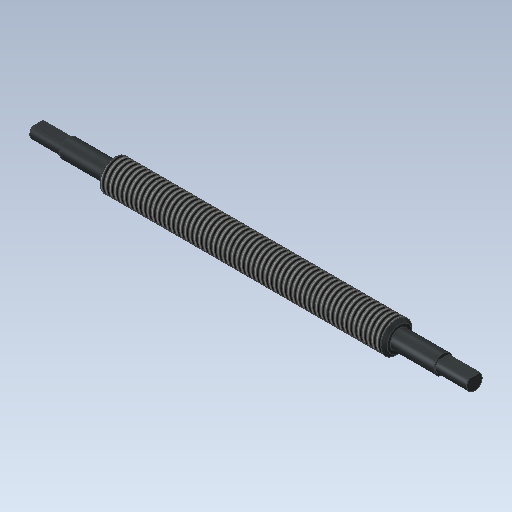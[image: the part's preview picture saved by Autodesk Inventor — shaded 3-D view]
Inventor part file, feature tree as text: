
AUTODESK INVENTOR PART (.ipt)
format: ipt  version: 2020 (Build 240168000, 168)  size: 140,288 bytes
history: native  units: mm
features: extrude x3, sketch x3, thread x1, chamfer x1, mirror x1
ambient origin geometry x8: Origin, YZ Plane, XZ Plane, XY Plane, X Axis, Y Axis, Z Axis, Center Point
bodies: Solid1 (feature_tree)
feature tree (9):
  extrude  "Extrusion1"  Depth=46.0mm TaperAngle=0.0deg
  thread  "Thread1"  [1 undecoded]
  chamfer  "Chamfer1"  Distance=1.0mm Angle=45.0deg
  extrude  "Extrusion2"  Depth=14.0mm TaperAngle=0.0deg
  extrude  "Extrusion3"  Depth=10.0mm
  mirror  "Mirror1"
  sketch  "Sketch1"  dims[d0=10.0mm d1=46.0mm d2=0.0mm d3=10.0mm d4=0.0mm d5=1.0mm d6=2.0mm d7=45.0deg]
  sketch  "Sketch2"  dims[d8=6.0mm d9=14.0mm d10=0.0mm]
  sketch  "Sketch3"  dims[d11=5.0mm d12=1.8mm d13=10.0mm d14=0.0mm]
note: 1 required parameter value undecoded (feature->parameter linkage not recoverable at this tier; creation-order binding heuristic only, values carry confidence <= 0.55)
